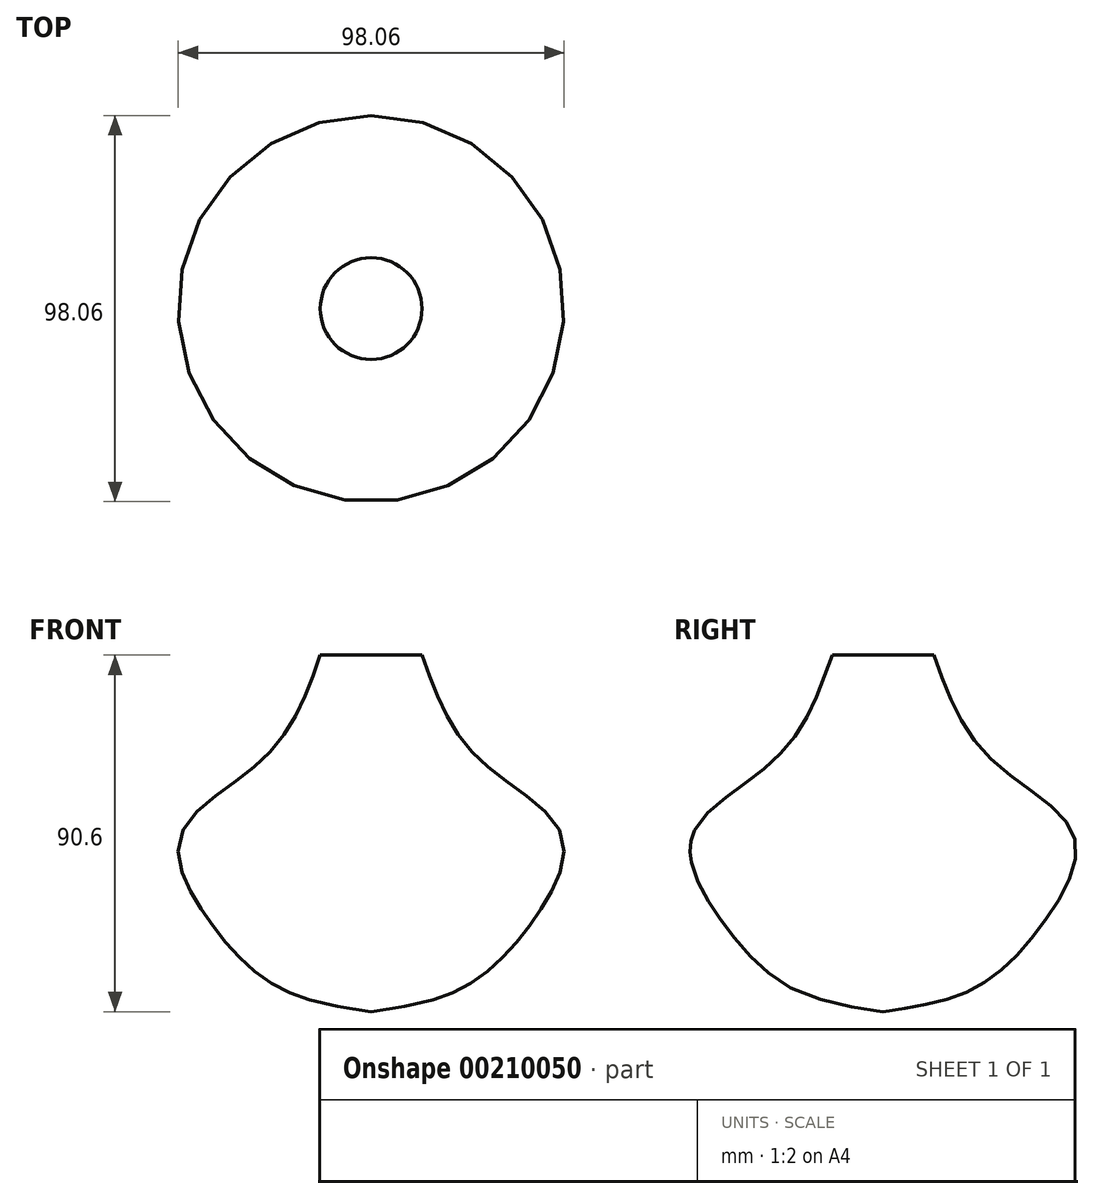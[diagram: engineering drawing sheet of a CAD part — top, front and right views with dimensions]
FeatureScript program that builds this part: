
annotation { "Feature Type Name" : "Feature", "Feature Type Description" : "" }
export const myFeature = defineFeature(function(context is Context, id is Id, definition is map)
    precondition{}
    {
        {
            var Q0;
            Q0=qCreatedBy(makeId("Right.planeOp"),FACE);
            var sketch = newSketch(context, id + "F0", { "sketchPlane" : qUnion([Q0])});
            skFitSpline(sketch, "E0", {"points": [v(12.91, 40.46) * mm, v(26.84, 14.63) * mm, v(48.43, -5.35) * mm, v(40.76, -27.54) * mm, v(23, -44.3) * mm, v(0, -50.14) * mm], "startDerivative": vector(46.02, -131.08) * mm, "endDerivative": vector(-127.1, -18.48) * mm});
            skLineSegment(sketch, "E1", {"start": v(0, 60.03) * mm, "end": v(0, 36.42) * mm});
            skSolve(sketch);
        }
        {
            var Q0;
            Q0=sQuery(id+"F0.wireOp",EDGE,"E0");
            var Q1;
            Q1=sQuery(id+"F0.wireOp",EDGE,"E1");
            revolve(context, id + "F1", {"bodyType" : ToolBodyType.SURFACE, "surfaceEntities" : qUnion([Q0]), "axis" : qUnion([Q1]), "revolveType" : RevolveType.FULL});
        }
    });
